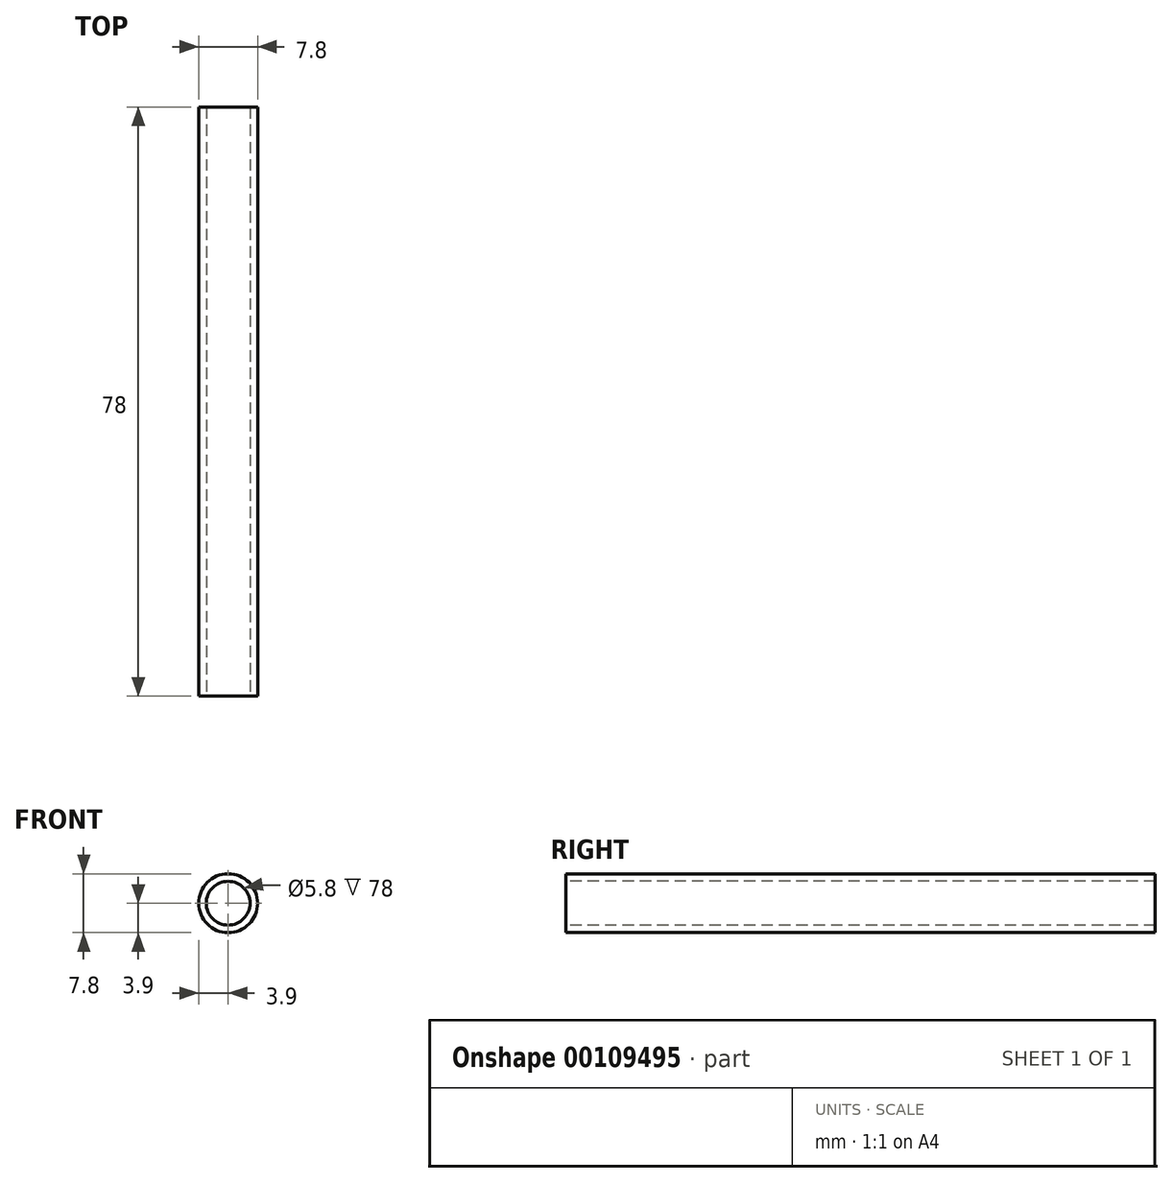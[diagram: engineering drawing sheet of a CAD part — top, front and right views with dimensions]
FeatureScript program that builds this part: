
annotation { "Feature Type Name" : "Feature", "Feature Type Description" : "" }
export const myFeature = defineFeature(function(context is Context, id is Id, definition is map)
    precondition{}
    {
        {
            var Q0;
            Q0=qCreatedBy(makeId("Top.planeOp"),FACE);
            var sketch = newSketch(context, id + "F0", { "sketchPlane" : qUnion([Q0])});
            skLineSegment(sketch, "E0", {"start": v(0, 0) * mm, "end": v(0, 78) * mm, "construction": true});
            skLineSegment(sketch, "E1.bottom", {"start": v(2.9, 0) * mm, "end": v(3.9, 0) * mm});
            skLineSegment(sketch, "E1.top", {"start": v(2.9, 78) * mm, "end": v(3.9, 78) * mm});
            skLineSegment(sketch, "E1.left", {"start": v(2.9, 0) * mm, "end": v(2.9, 78) * mm});
            skLineSegment(sketch, "E1.right", {"start": v(3.9, 0) * mm, "end": v(3.9, 78) * mm});
            skSolve(sketch);
        }
        {
            var Q0;
            Q0=qSketchRegion(id+"F0",true);
            var Q1;
            Q1=sQuery(id+"F0.wireOp",EDGE,"E0");
            revolve(context, id + "F1", {"entities" : qUnion([Q0]), "axis" : qUnion([Q1]), "revolveType" : RevolveType.FULL});
        }
    });
